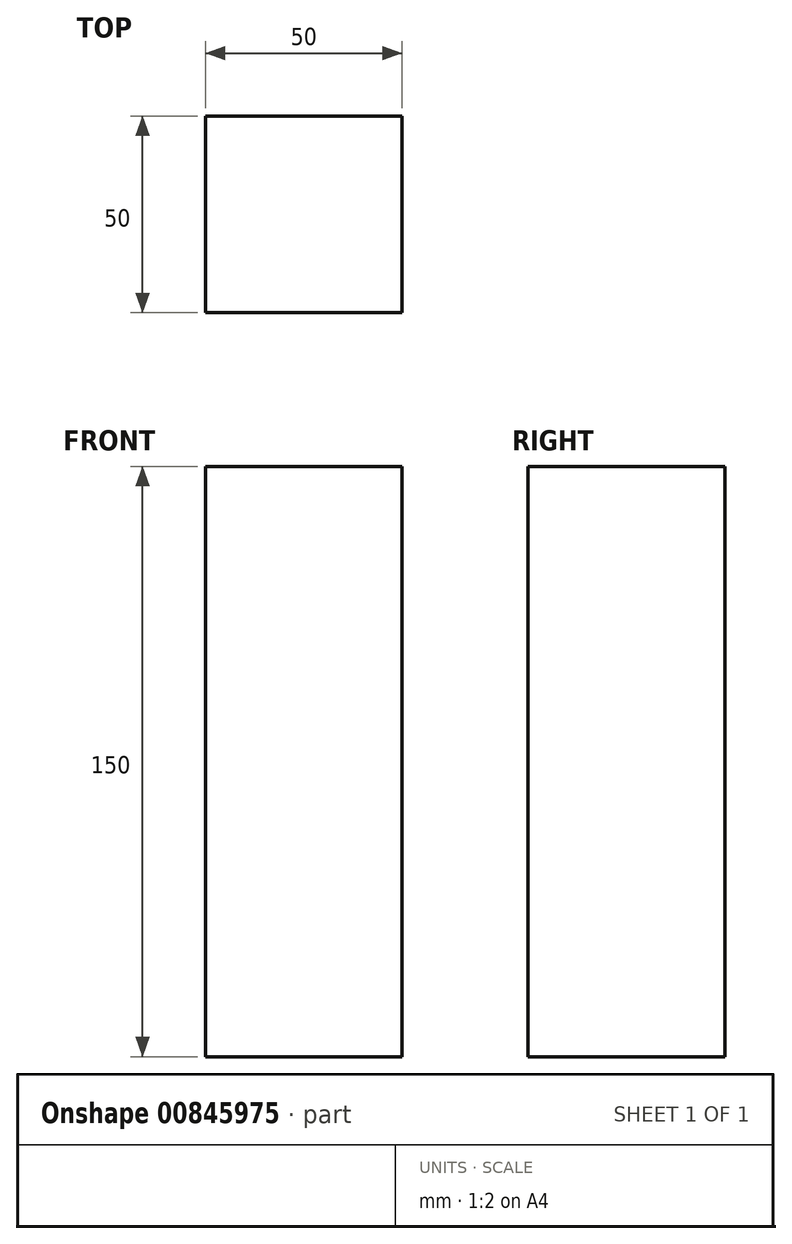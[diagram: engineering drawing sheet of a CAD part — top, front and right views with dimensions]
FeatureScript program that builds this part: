
annotation { "Feature Type Name" : "Feature", "Feature Type Description" : "" }
export const myFeature = defineFeature(function(context is Context, id is Id, definition is map)
    precondition{}
    {
        {
            var Q0;
            Q0=qCreatedBy(makeId("Top.planeOp"),FACE);
            var sketch = newSketch(context, id + "F0", { "sketchPlane" : qUnion([Q0])});
            skLineSegment(sketch, "E0.bottom", {"start": v(25, 25) * mm, "end": v(-25, 25) * mm});
            skLineSegment(sketch, "E0.top", {"start": v(25, -25) * mm, "end": v(-25, -25) * mm});
            skLineSegment(sketch, "E0.left", {"start": v(25, 25) * mm, "end": v(25, -25) * mm});
            skLineSegment(sketch, "E0.right", {"start": v(-25, 25) * mm, "end": v(-25, -25) * mm});
            skPoint(sketch, "E0.middle", {"position": v(0, 0) * mm});
            skSolve(sketch);
        }
        {
            var Q0;
            Q0=makeQuery(id+"F0.imprint","IMPRINT",FACE,{"disambiguationData":[TD([[makeQuery(id+"F0.imprint","IMPRINT",EDGE,{"derivedFrom":sQuery(id+"F0.wireOp",EDGE,"E0.bottom")}),1.0]])]});
            extrude(context, id + "F1", {"entities" : qUnion([Q0]), "depth" : 150 * mm, "offsetDistance" : 25 * mm});
        }
    });
